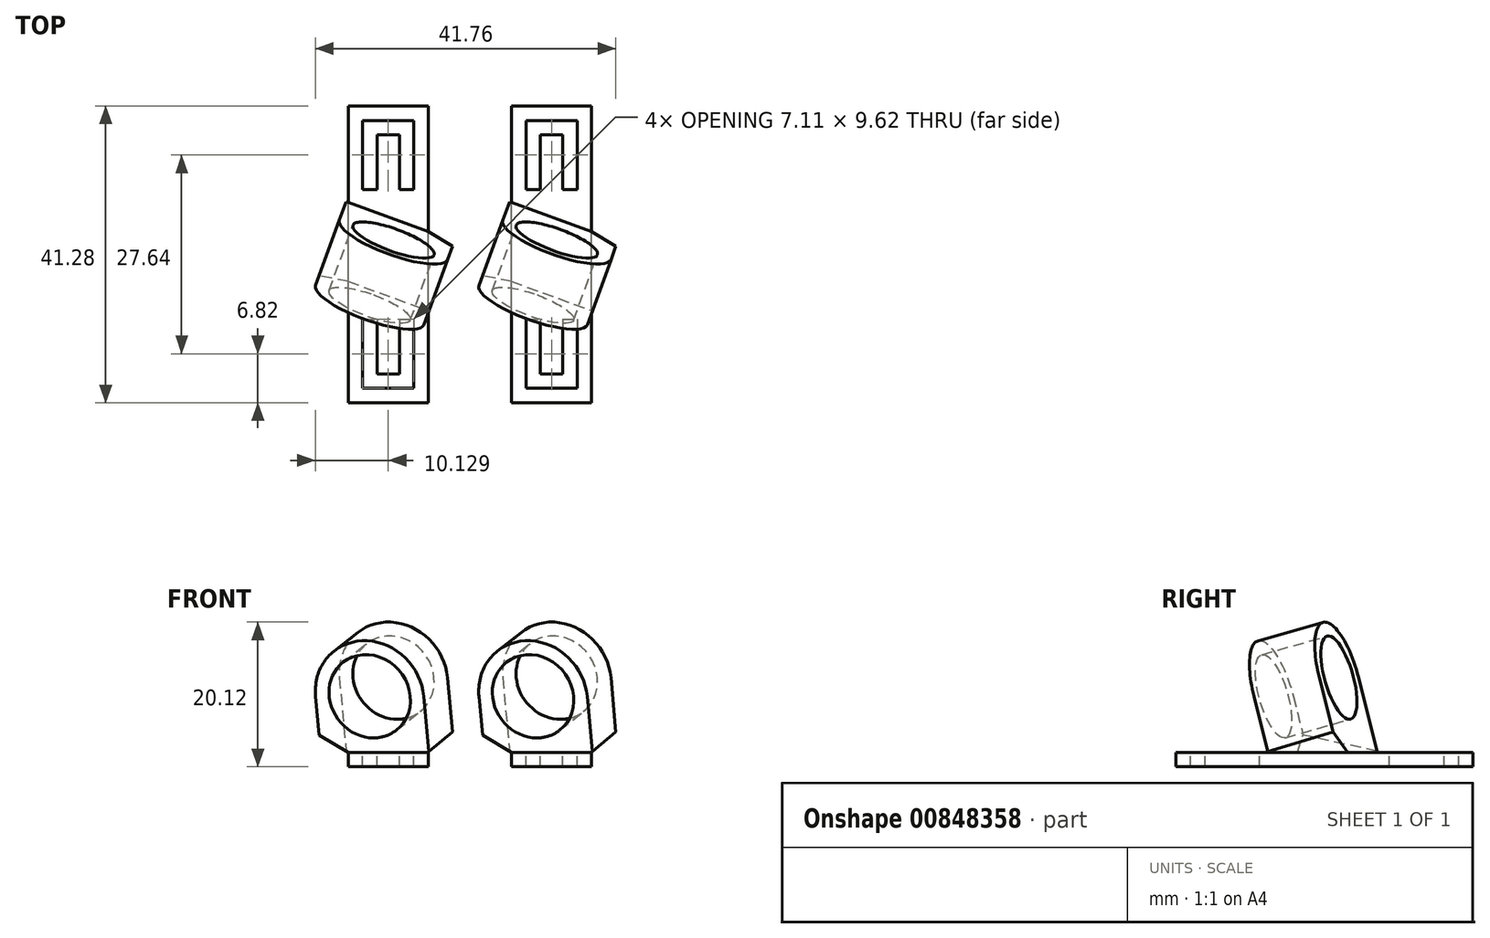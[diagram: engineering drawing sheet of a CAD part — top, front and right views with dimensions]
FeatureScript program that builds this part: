
annotation { "Feature Type Name" : "Feature", "Feature Type Description" : "" }
export const myFeature = defineFeature(function(context is Context, id is Id, definition is map)
    precondition{}
    {
        {
            var Q0;
            Q0=qCreatedBy(makeId("Front.planeOp"),FACE);
            var sketch = newSketch(context, id + "F0", { "sketchPlane" : qUnion([Q0])});
            skLineSegment(sketch, "E0.bottom", {"start": v(-63.63, 0) * mm, "end": v(-52.52, 0) * mm});
            skLineSegment(sketch, "E0.top", {"start": v(-63.63, 2) * mm, "end": v(-52.52, 2) * mm});
            skLineSegment(sketch, "E0.left", {"start": v(-63.63, 0) * mm, "end": v(-63.63, 2) * mm});
            skLineSegment(sketch, "E0.right", {"start": v(-52.52, 0) * mm, "end": v(-52.52, 2) * mm});
            skLineSegment(sketch, "E1", {"start": v(-63.63, 1) * mm, "end": v(-52.52, 1) * mm, "construction": true});
            skLineSegment(sketch, "E2", {"start": v(-58.07, 0) * mm, "end": v(-58.07, 2) * mm, "construction": true});
            skPoint(sketch, "E3.orphan", {"position": v(-63.1, 9.7) * mm});
            skPoint(sketch, "E4.orphan", {"position": v(-61.67, 8.3) * mm});
            skPoint(sketch, "E5.end.orphan", {"position": v(-57.73, 8.3) * mm});
            skPoint(sketch, "E6.orphan", {"position": v(-56.3, 9.7) * mm});
            skPoint(sketch, "E7.orphan", {"position": v(-58.07, 12.73) * mm});
            skPoint(sketch, "E8.center.orphan", {"position": v(-58.07, 6.37) * mm});
            skCircle(sketch, "E9", {"center": v(-58.07, 11.45) * mm, "radius": 6 * mm});
            skCircle(sketch, "E10", {"center": v(-58.07, 11.45) * mm, "radius": 8 * mm});
            skLineSegment(sketch, "E11", {"start": v(-66.07, 11.45) * mm, "end": v(-66.07, 2) * mm});
            skLineSegment(sketch, "E12", {"start": v(-66.07, 2) * mm, "end": v(-50.07, 2) * mm});
            skLineSegment(sketch, "E13", {"start": v(-50.07, 2) * mm, "end": v(-50.07, 11.45) * mm});
            skPoint(sketch, "E14.end.orphan", {"position": v(-63, 5.16) * mm});
            skPoint(sketch, "E15.end.orphan", {"position": v(-51.9, 5.16) * mm});
            skSolve(sketch);
        }
        {
            var Q0;
            Q0=makeQuery(id+"F0.imprint","IMPRINT",FACE,{"disambiguationData":[TD([[makeQuery(id+"F0.imprint","IMPRINT",EDGE,{"derivedFrom":sQuery(id+"F0.wireOp",EDGE,"E0.bottom")}),1.0]])]});
            extrude(context, id + "F1", {"entities" : qUnion([Q0]), "endBound" : BoundingType.SYMMETRIC, "depth" : 41.28 * mm});
        }
        {
            var Q0;
            Q0=makeQuery(id+"F0.imprint","IMPRINT",FACE,{"disambiguationData":[TD([[makeQuery(id+"F0.imprint","IMPRINT",EDGE,{"derivedFrom":sQuery(id+"F0.wireOp",EDGE,"E9")}),-1.0]])]});
            var Q1;
            {var subQ1=sQuery(id+"F0.wireOp",EDGE,"E0.top");Q1=makeQuery(id+"F0.imprint","IMPRINT",FACE,{"disambiguationData":[TD([[makeQuery(id+"F0.imprint","IMPRINT",EDGE,{"derivedFrom":subQ1}),1.0]])]});}
            var Q2;
            Q2=sQuery(id+"F0.wireOp",EDGE,"E9");
            var Q3;
            Q3=sQuery(id+"F0.wireOp",EDGE,"E10");
            var Q4;
            Q4=sQuery(id+"F0.wireOp",EDGE,"E13");
            var Q5;
            Q5=sQuery(id+"F0.wireOp",EDGE,"E12");
            var Q6;
            Q6=sQuery(id+"F0.wireOp",EDGE,"E11");
            extrude(context, id + "F2", {"entities" : qUnion([Q0, Q1]), "surfaceEntities" : qUnion([Q2, Q3, Q4, Q5, Q6]), "endBound" : BoundingType.SYMMETRIC, "depth" : 10 * mm});
        }
        {
            var Q0;
            Q0=makeQuery(id+"F2.opExtrude","SWEPT_BODY",BODY,{"disambiguationData":[OSD([sQuery(id+"F0.wireOp",EDGE,"E0.top"),sQuery(id+"F0.wireOp",EDGE,"E9"),sQuery(id+"F0.wireOp",EDGE,"E10"),sQuery(id+"F0.wireOp",EDGE,"E11"),sQuery(id+"F0.wireOp",EDGE,"E12"),sQuery(id+"F0.wireOp",EDGE,"E13")])]});
            var Q1;
            Q1=sQuery(id+"F0.wireOp",EDGE,"E1");
            transform(context, id + "F3", {"entities" : qUnion([Q0]), "transformType" : TransformType.ROTATION, "transformAxis" : qUnion([Q1]), "angle" : 15 * degree, "makeCopy" : false});
        }
        {
            var Q0;
            Q0=makeQuery(id+"F2.opExtrude","SWEPT_BODY",BODY,{"disambiguationData":[OSD([sQuery(id+"F0.wireOp",EDGE,"E0.top"),sQuery(id+"F0.wireOp",EDGE,"E9"),sQuery(id+"F0.wireOp",EDGE,"E10"),sQuery(id+"F0.wireOp",EDGE,"E11"),sQuery(id+"F0.wireOp",EDGE,"E12"),sQuery(id+"F0.wireOp",EDGE,"E13")])]});
            var Q1;
            Q1=sQuery(id+"F0.wireOp",EDGE,"E2");
            transform(context, id + "F4", {"entities" : qUnion([Q0]), "transformType" : TransformType.ROTATION, "transformAxis" : qUnion([Q1]), "angle" : 20 * degree, "oppositeDirection" : true, "makeCopy" : false});
        }
        {
            var Q0;
            Q0=makeQuery(id+"F2.opExtrude","SWEPT_FACE",FACE,{"disambiguationData":[OSD([sQuery(id+"F0.wireOp",EDGE,"E0.top"),sQuery(id+"F0.wireOp",EDGE,"E12")])]});
            var Q1;
            Q1=makeQuery(id+"F1.opExtrude","SWEPT_FACE",FACE,{"disambiguationData":[OSD([sQuery(id+"F0.wireOp",EDGE,"E0.bottom")])]});
            extrude(context, id + "F5", {"entities" : qUnion([Q0]), "endBound" : BoundingType.UP_TO_SURFACE, "endBoundEntityFace" : qUnion([Q1]), "depth" : 25 * mm});
        }
        {
            var Q0;
            Q0=makeQuery(id+"F1.opExtrude","SWEPT_FACE",FACE,{"disambiguationData":[OSD([sQuery(id+"F0.wireOp",EDGE,"E0.left")])]});
            extrude(context, id + "F6", {"entities" : qUnion([Q0]), "operationType" : NewBodyOperationType.REMOVE, "depth" : 6.9 * mm});
        }
        {
            var Q0;
            Q0=makeQuery(id+"F1.opExtrude","SWEPT_FACE",FACE,{"disambiguationData":[OSD([sQuery(id+"F0.wireOp",EDGE,"E0.right")])]});
            extrude(context, id + "F7", {"entities" : qUnion([Q0]), "operationType" : NewBodyOperationType.REMOVE, "depth" : 25 * mm});
        }
        {
            var Q0;
            Q0=makeQuery(id+"F1.opExtrude","SWEPT_BODY",BODY,{"disambiguationData":[OSD([sQuery(id+"F0.wireOp",EDGE,"E0.bottom"),sQuery(id+"F0.wireOp",EDGE,"E0.top"),sQuery(id+"F0.wireOp",EDGE,"E0.left"),sQuery(id+"F0.wireOp",EDGE,"E0.right")])]});
            var Q1;
            Q1=makeQuery(id+"F2.opExtrude","SWEPT_BODY",BODY,{"disambiguationData":[OSD([sQuery(id+"F0.wireOp",EDGE,"E0.top"),sQuery(id+"F0.wireOp",EDGE,"E9"),sQuery(id+"F0.wireOp",EDGE,"E10"),sQuery(id+"F0.wireOp",EDGE,"E11"),sQuery(id+"F0.wireOp",EDGE,"E12"),sQuery(id+"F0.wireOp",EDGE,"E13")])]});
            var Q2;
            Q2=makeQuery(id+"F5.opExtrude","SWEPT_BODY",BODY,{"disambiguationData":[OSD([sQuery(id+"F0.wireOp",EDGE,"E0.top"),sQuery(id+"F0.wireOp",EDGE,"E12")])]});
            booleanBodies(context, id + "F8", {"operationType" : BooleanOperationType.UNION, "tools" : qUnion([Q0, Q1, Q2])});
        }
        {
            var Q0;
            Q0=makeQuery(id+"F1.opExtrude","SWEPT_BODY",BODY,{"disambiguationData":[OSD([sQuery(id+"F0.wireOp",EDGE,"E0.bottom"),sQuery(id+"F0.wireOp",EDGE,"E0.top"),sQuery(id+"F0.wireOp",EDGE,"E0.left"),sQuery(id+"F0.wireOp",EDGE,"E0.right")])]});
            transform(context, id + "F9", {"entities" : qUnion([Q0]), "transformType" : TransformType.TRANSLATION_3D, "dx" : 28.1 * mm, "dy" : 0 * mm, "dz" : 0 * mm, "makeCopy" : true});
        }
        {
            var Q0;
            Q0=makeQuery(id+"F1.opExtrude","CAP_FACE",FACE,{"disambiguationData":[OSD([sQuery(id+"F0.wireOp",EDGE,"E0.bottom"),sQuery(id+"F0.wireOp",EDGE,"E0.top"),sQuery(id+"F0.wireOp",EDGE,"E0.left"),sQuery(id+"F0.wireOp",EDGE,"E0.right")])],"isStart":false});
            var sketch = newSketch(context, id + "F10", { "sketchPlane" : qUnion([Q0])});
            skLineSegment(sketch, "E16", {"start": v(-52.52, 2) * mm, "end": v(-47.6, 6.13) * mm});
            skLineSegment(sketch, "E17", {"start": v(-47.6, 6.13) * mm, "end": v(-47.6, 0) * mm});
            skLineSegment(sketch, "E18", {"start": v(-47.6, 0) * mm, "end": v(-52.52, 0) * mm});
            skLineSegment(sketch, "E19", {"start": v(-52.52, 0) * mm, "end": v(-52.52, 2) * mm});
            skLineSegment(sketch, "E20", {"start": v(-63.63, 2) * mm, "end": v(-68.91, 5.14) * mm});
            skLineSegment(sketch, "E21", {"start": v(-68.91, 5.14) * mm, "end": v(-68.91, 0) * mm});
            skLineSegment(sketch, "E22", {"start": v(-68.91, 0) * mm, "end": v(-63.63, 0) * mm});
            skLineSegment(sketch, "E23", {"start": v(-63.63, 0) * mm, "end": v(-63.63, 2) * mm});
            skSolve(sketch);
        }
        {
            var Q0;
            Q0=qSketchRegion(id+"F10",true);
            extrude(context, id + "F11", {"entities" : qUnion([Q0]), "operationType" : NewBodyOperationType.REMOVE, "oppositeDirection" : true, "depth" : 25 * mm});
        }
        {
            var Q0;
            Q0=qSketchRegion(id+"F10",true);
            extrude(context, id + "F12", {"entities" : qUnion([Q0]), "operationType" : NewBodyOperationType.REMOVE, "oppositeDirection" : true, "depth" : 31 * mm});
        }
        {
            var Q0;
            Q0=makeQuery(id+"F9.opPattern","COPY",BODY,{"derivedFrom":makeQuery(id+"F1.opExtrude","SWEPT_BODY",BODY,{"disambiguationData":[OSD([sQuery(id+"F0.wireOp",EDGE,"E0.bottom"),sQuery(id+"F0.wireOp",EDGE,"E0.top"),sQuery(id+"F0.wireOp",EDGE,"E0.left"),sQuery(id+"F0.wireOp",EDGE,"E0.right")])]}),"instanceName":"1"});
            deleteBodies(context, id + "F13", {"entities" : qUnion([Q0])});
        }
        {
            var Q0;
            {var subQ2=sQuery(id+"F0.wireOp",EDGE,"E12");var subQ4=sQuery(id+"F0.wireOp",EDGE,"E0.top");Q0=makeQuery(id+"F8.opBoolean","SPLIT",FACE,{"disambiguationData":[TD([makeQuery(id+"F5.opExtrude","SWEPT_FACE",FACE,{"disambiguationData":[OSD([subQ4,subQ2]),TDD([makeQuery(id+"F2.opExtrude","CAP_EDGE",EDGE,{"disambiguationData":[OSD([subQ4,subQ2])],"isStart":false})])]})])],"derivedFrom":makeQuery(id+"F1.opExtrude","SWEPT_FACE",FACE,{"disambiguationData":[OSD([subQ4])]})});}
            var sketch = newSketch(context, id + "F14", { "sketchPlane" : qUnion([Q0])});
            skLineSegment(sketch, "E24.bottom", {"start": v(-61.63, -9) * mm, "end": v(-59.62, -9) * mm});
            skLineSegment(sketch, "E24.top", {"start": v(-61.63, -18.63) * mm, "end": v(-54.52, -18.63) * mm});
            skLineSegment(sketch, "E24.left", {"start": v(-61.63, -9) * mm, "end": v(-61.63, -18.63) * mm});
            skLineSegment(sketch, "E24.right", {"start": v(-54.52, -9) * mm, "end": v(-54.52, -18.63) * mm});
            skLineSegment(sketch, "E25.top", {"start": v(-59.62, -16.62) * mm, "end": v(-56.53, -16.62) * mm});
            skLineSegment(sketch, "E25.left", {"start": v(-59.62, -9) * mm, "end": v(-59.62, -16.62) * mm});
            skLineSegment(sketch, "E25.right", {"start": v(-56.53, -9) * mm, "end": v(-56.53, -16.62) * mm});
            skLineSegment(sketch, "E26.trimOffspring", {"start": v(-56.53, -9) * mm, "end": v(-54.52, -9) * mm});
            skLineSegment(sketch, "E27.MirrorCS", {"start": v(-61.63, 18.63) * mm, "end": v(-54.52, 18.63) * mm});
            skLineSegment(sketch, "E28.MirrorCS", {"start": v(-54.52, 9) * mm, "end": v(-54.52, 18.63) * mm});
            skLineSegment(sketch, "E29.MirrorCS", {"start": v(-56.53, 9) * mm, "end": v(-56.53, 16.62) * mm});
            skLineSegment(sketch, "E30.MirrorCS", {"start": v(-59.62, 16.62) * mm, "end": v(-56.53, 16.62) * mm});
            skLineSegment(sketch, "E31.MirrorCS", {"start": v(-59.62, 9) * mm, "end": v(-59.62, 16.62) * mm});
            skLineSegment(sketch, "E32.MirrorCS", {"start": v(-61.63, 9) * mm, "end": v(-61.63, 18.63) * mm});
            skLineSegment(sketch, "E33.MirrorCS", {"start": v(-61.63, 9) * mm, "end": v(-59.62, 9) * mm});
            skLineSegment(sketch, "E34.MirrorCS", {"start": v(-56.53, 9) * mm, "end": v(-54.52, 9) * mm});
            skSolve(sketch);
        }
        {
            var Q0;
            Q0=qSketchRegion(id+"F14",true);
            extrude(context, id + "F15", {"entities" : qUnion([Q0]), "operationType" : NewBodyOperationType.REMOVE, "oppositeDirection" : true, "depth" : 25 * mm});
        }
        {
            var Q0;
            Q0=makeQuery(id+"F1.opExtrude","SWEPT_BODY",BODY,{"disambiguationData":[OSD([sQuery(id+"F0.wireOp",EDGE,"E0.bottom"),sQuery(id+"F0.wireOp",EDGE,"E0.top"),sQuery(id+"F0.wireOp",EDGE,"E0.left"),sQuery(id+"F0.wireOp",EDGE,"E0.right")])]});
            transform(context, id + "F16", {"entities" : qUnion([Q0]), "transformType" : TransformType.TRANSLATION_3D, "dx" : 22.7 * mm, "dy" : 0 * mm, "dz" : 0 * mm, "makeCopy" : true});
        }
        {
            var Q0;
            Q0=makeQuery(id+"F1.opExtrude","SWEPT_BODY",BODY,{"disambiguationData":[OSD([sQuery(id+"F0.wireOp",EDGE,"E0.bottom"),sQuery(id+"F0.wireOp",EDGE,"E0.top"),sQuery(id+"F0.wireOp",EDGE,"E0.left"),sQuery(id+"F0.wireOp",EDGE,"E0.right")])]});
            transform(context, id + "F17", {"entities" : qUnion([Q0]), "transformType" : TransformType.TRANSLATION_3D, "dx" : 43.6 * mm, "dy" : 0 * mm, "dz" : 0 * mm, "makeCopy" : true});
        }
        {
            var Q0;
            Q0=makeQuery(id+"F17.opPattern","COPY",BODY,{"derivedFrom":makeQuery(id+"F1.opExtrude","SWEPT_BODY",BODY,{"disambiguationData":[OSD([sQuery(id+"F0.wireOp",EDGE,"E0.bottom"),sQuery(id+"F0.wireOp",EDGE,"E0.top"),sQuery(id+"F0.wireOp",EDGE,"E0.left"),sQuery(id+"F0.wireOp",EDGE,"E0.right")])]}),"instanceName":"1"});
            deleteBodies(context, id + "F18", {"entities" : qUnion([Q0])});
        }
    });
